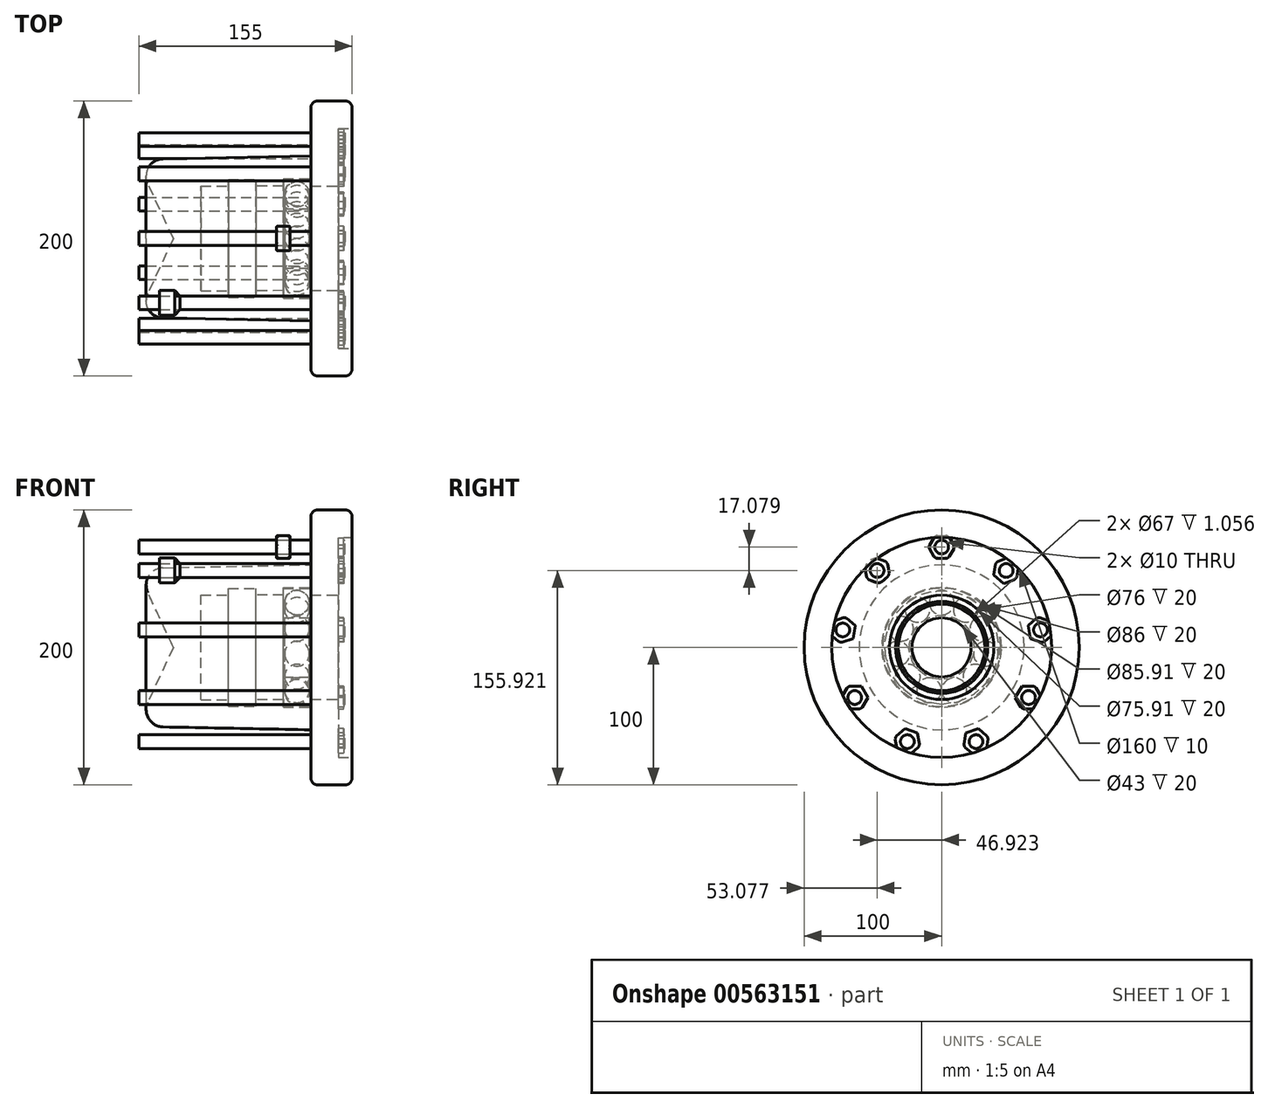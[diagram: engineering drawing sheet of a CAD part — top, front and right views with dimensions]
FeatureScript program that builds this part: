
annotation { "Feature Type Name" : "Feature", "Feature Type Description" : "" }
export const myFeature = defineFeature(function(context is Context, id is Id, definition is map)
    precondition{}
    {
        {
            var Q0;
            Q0=qCreatedBy(makeId("Front.planeOp"),FACE);
            var sketch = newSketch(context, id + "F0", { "sketchPlane" : qUnion([Q0])});
            skLineSegment(sketch, "E0", {"start": v(30, 100) * mm, "end": v(0, 100) * mm});
            skLineSegment(sketch, "E1", {"start": v(0, 100) * mm, "end": v(0, 60) * mm});
            skLineSegment(sketch, "E2.1", {"start": v(30, 80) * mm, "end": v(20, 80) * mm});
            skLineSegment(sketch, "E3", {"start": v(30, 100) * mm, "end": v(30, 80) * mm});
            skLineSegment(sketch, "E4", {"start": v(-100, 0) * mm, "end": v(-80, 0) * mm});
            skLineSegment(sketch, "E5", {"start": v(-80, 38) * mm, "end": v(-80, 0) * mm});
            skLineSegment(sketch, "E6", {"start": v(-50, 0) * mm, "end": v(-50, 38) * mm, "construction": true});
            skLineSegment(sketch, "E7", {"start": v(-80, 38) * mm, "end": v(-60, 38) * mm});
            skLineSegment(sketch, "E8", {"start": v(-60, 38) * mm, "end": v(-60, 43) * mm});
            skLineSegment(sketch, "E9", {"start": v(-60, 43) * mm, "end": v(-40, 43) * mm});
            skLineSegment(sketch, "E10", {"start": v(-40, 43) * mm, "end": v(-40, 38) * mm});
            skLineSegment(sketch, "E11", {"start": v(-20, 37.96) * mm, "end": v(-20, 42.96) * mm});
            skLineSegment(sketch, "E12", {"start": v(-20, 42.96) * mm, "end": v(0, 42.96) * mm});
            skLineSegment(sketch, "E13", {"start": v(0, 42.96) * mm, "end": v(0, 37.96) * mm});
            skLineSegment(sketch, "E14", {"start": v(0, 37.96) * mm, "end": v(20, 37.96) * mm});
            skLineSegment(sketch, "E15", {"start": v(20, 37.96) * mm, "end": v(20, 80) * mm});
            skLineSegment(sketch, "E16", {"start": v(-40, 38) * mm, "end": v(-20, 37.96) * mm});
            skLineSegment(sketch, "E17", {"start": v(0, 60) * mm, "end": v(-126.66, 57.5) * mm});
            skLineSegment(sketch, "E18", {"start": v(-126.66, 57.5) * mm, "end": v(-100, 0) * mm});
            skLineSegment(sketch, "E19", {"start": v(0, 0) * mm, "end": v(-33.89, 0) * mm, "construction": true});
            skSolve(sketch);
        }
        {
            var Q0;
            Q0=makeQuery(id+"F0.imprint","IMPRINT",FACE,{"disambiguationData":[TD([[makeQuery(id+"F0.imprint","IMPRINT",EDGE,{"derivedFrom":sQuery(id+"F0.wireOp",EDGE,"E0")}),1.0]])]});
            var Q1;
            Q1=sQuery(id+"F0.wireOp",EDGE,"E19");
            revolve(context, id + "F1", {"entities" : qUnion([Q0]), "axis" : qUnion([Q1]), "revolveType" : RevolveType.FULL});
        }
        {
            var Q0;
            Q0=makeQuery(id+"F1.opRevolve","SWEPT_EDGE",EDGE,{"disambiguationData":[OSD([sQuery(id+"F0.wireOp",EDGE,"jqeio1sC-Fs1J-a6Xr-Syng-ZmbF2VibZQXp"),sQuery(id+"F0.wireOp",EDGE,"7w0ZohrY-VkOi-IecW-S3rd-IawNJfoClKoL")])]});
            var Q1;
            Q1=makeQuery(id+"F1.opRevolve","SWEPT_EDGE",EDGE,{"disambiguationData":[OSD([sQuery(id+"F0.wireOp",EDGE,"E0"),sQuery(id+"F0.wireOp",EDGE,"E1")])]});
            var Q2;
            Q2=makeQuery(id+"F1.opRevolve","SWEPT_EDGE",EDGE,{"disambiguationData":[OSD([sQuery(id+"F0.wireOp",EDGE,"8LsLQbTB-hIyZ-haP9-eTfZ-4Z8Wfnln9Azo"),sQuery(id+"F0.wireOp",EDGE,"E0")])]});
            fillet(context, id + "F2", {"entities" : qUnion([Q0, Q1, Q2]), "radius" : 5 * mm, "tangentPropagation" : true, "allowEdgeOverflow" : false});
        }
        {
            var Q0;
            Q0=qCreatedBy(makeId("Right.planeOp"),FACE);
            var sketch = newSketch(context, id + "F3", { "sketchPlane" : qUnion([Q0])});
            skLineSegment(sketch, "E20", {"start": v(0, 0) * mm, "end": v(0, 73) * mm, "construction": true});
            skCircle(sketch, "E21", {"center": v(0, 73) * mm, "radius": 5 * mm});
            skCircle(sketch, "E22.1.0", {"center": v(-46.92, 55.92) * mm, "radius": 5 * mm});
            skCircle(sketch, "E22.2.0", {"center": v(-71.9, 12.68) * mm, "radius": 5 * mm});
            skCircle(sketch, "E22.3.0", {"center": v(-63.22, -36.5) * mm, "radius": 5 * mm});
            skCircle(sketch, "E22.4.0", {"center": v(-24.97, -68.6) * mm, "radius": 5 * mm});
            skCircle(sketch, "E22.5.0", {"center": v(24.97, -68.6) * mm, "radius": 5 * mm});
            skCircle(sketch, "E22.6.0", {"center": v(63.22, -36.5) * mm, "radius": 5 * mm});
            skCircle(sketch, "E22.7.0", {"center": v(71.9, 12.68) * mm, "radius": 5 * mm});
            skCircle(sketch, "E22.8.0", {"center": v(46.92, 55.92) * mm, "radius": 5 * mm});
            skPoint(sketch, "E22.center", {"position": v(0, 0) * mm});
            skCircle(sketch, "E23.cCircle", {"center": v(0, 73) * mm, "radius": 8.37 * mm, "construction": true});
            skLineSegment(sketch, "E23.0", {"start": v(4.83, 64.63) * mm, "end": v(-4.83, 64.63) * mm});
            skLineSegment(sketch, "E23.1", {"start": v(-4.83, 64.63) * mm, "end": v(-9.66, 73) * mm});
            skLineSegment(sketch, "E23.2", {"start": v(-9.66, 73) * mm, "end": v(-4.83, 81.37) * mm});
            skLineSegment(sketch, "E23.3", {"start": v(-4.83, 81.37) * mm, "end": v(4.83, 81.37) * mm});
            skLineSegment(sketch, "E23.4", {"start": v(4.83, 81.37) * mm, "end": v(9.66, 73) * mm});
            skLineSegment(sketch, "E23.5", {"start": v(9.66, 73) * mm, "end": v(4.83, 64.63) * mm});
            skPoint(sketch, "E23.0.midPoint", {"position": v(0, 64.63) * mm});
            skCircle(sketch, "E24.1.0", {"center": v(-63.22, -36.5) * mm, "radius": 8.37 * mm, "construction": true});
            skLineSegment(sketch, "E24.1.1", {"start": v(-68.05, -44.87) * mm, "end": v(-72.88, -36.5) * mm});
            skLineSegment(sketch, "E24.1.2", {"start": v(-58.39, -44.87) * mm, "end": v(-68.05, -44.87) * mm});
            skLineSegment(sketch, "E24.1.3", {"start": v(-72.88, -36.5) * mm, "end": v(-68.05, -28.13) * mm});
            skCircle(sketch, "E24.2.0", {"center": v(63.22, -36.5) * mm, "radius": 8.37 * mm, "construction": true});
            skLineSegment(sketch, "E24.2.1", {"start": v(72.88, -36.5) * mm, "end": v(68.05, -44.87) * mm});
            skLineSegment(sketch, "E24.2.2", {"start": v(68.05, -28.13) * mm, "end": v(72.88, -36.5) * mm});
            skLineSegment(sketch, "E24.2.3", {"start": v(68.05, -44.87) * mm, "end": v(58.39, -44.87) * mm});
            skLineSegment(sketch, "E25.1.0", {"start": v(-37.84, 52.62) * mm, "end": v(-45.25, 46.4) * mm});
            skLineSegment(sketch, "E25.1.1", {"start": v(-48.6, 65.44) * mm, "end": v(-39.52, 62.13) * mm});
            skCircle(sketch, "E25.1.2", {"center": v(-46.92, 55.92) * mm, "radius": 8.37 * mm, "construction": true});
            skLineSegment(sketch, "E25.1.4", {"start": v(-54.32, 49.71) * mm, "end": v(-56, 59.23) * mm});
            skLineSegment(sketch, "E25.1.5", {"start": v(-56, 59.23) * mm, "end": v(-48.6, 65.44) * mm});
            skLineSegment(sketch, "E25.1.6", {"start": v(-39.52, 62.13) * mm, "end": v(-37.84, 52.62) * mm});
            skLineSegment(sketch, "E25.1.7", {"start": v(-45.25, 46.4) * mm, "end": v(-54.32, 49.71) * mm});
            skPoint(sketch, "E25.1.8", {"position": v(-41.55, 49.51) * mm});
            skLineSegment(sketch, "E25.2.0", {"start": v(-62.81, 15.98) * mm, "end": v(-64.5, 6.47) * mm});
            skLineSegment(sketch, "E25.2.1", {"start": v(-79.3, 18.89) * mm, "end": v(-70.21, 22.2) * mm});
            skCircle(sketch, "E25.2.2", {"center": v(-71.9, 12.68) * mm, "radius": 8.37 * mm, "construction": true});
            skLineSegment(sketch, "E25.2.4", {"start": v(-73.57, 3.16) * mm, "end": v(-80.97, 9.37) * mm});
            skLineSegment(sketch, "E25.2.5", {"start": v(-80.97, 9.37) * mm, "end": v(-79.3, 18.89) * mm});
            skLineSegment(sketch, "E25.2.6", {"start": v(-70.21, 22.2) * mm, "end": v(-62.81, 15.98) * mm});
            skLineSegment(sketch, "E25.2.7", {"start": v(-64.5, 6.47) * mm, "end": v(-73.57, 3.16) * mm});
            skPoint(sketch, "E25.2.8", {"position": v(-63.65, 11.22) * mm});
            skLineSegment(sketch, "E25.3.0", {"start": v(-58.39, -28.13) * mm, "end": v(-53.56, -36.5) * mm});
            skLineSegment(sketch, "E25.3.6", {"start": v(-68.05, -28.13) * mm, "end": v(-58.39, -28.13) * mm});
            skLineSegment(sketch, "E25.3.7", {"start": v(-53.56, -36.5) * mm, "end": v(-58.39, -44.87) * mm});
            skPoint(sketch, "E25.3.8", {"position": v(-55.97, -32.32) * mm});
            skLineSegment(sketch, "E25.4.0", {"start": v(-26.65, -59.08) * mm, "end": v(-17.57, -62.39) * mm});
            skLineSegment(sketch, "E25.4.1", {"start": v(-32.37, -74.8) * mm, "end": v(-34.05, -65.3) * mm});
            skCircle(sketch, "E25.4.2", {"center": v(-24.97, -68.6) * mm, "radius": 8.37 * mm, "construction": true});
            skLineSegment(sketch, "E25.4.4", {"start": v(-15.89, -71.9) * mm, "end": v(-23.29, -78.11) * mm});
            skLineSegment(sketch, "E25.4.5", {"start": v(-23.29, -78.11) * mm, "end": v(-32.37, -74.8) * mm});
            skLineSegment(sketch, "E25.4.6", {"start": v(-34.05, -65.3) * mm, "end": v(-26.65, -59.08) * mm});
            skLineSegment(sketch, "E25.4.7", {"start": v(-17.57, -62.39) * mm, "end": v(-15.89, -71.9) * mm});
            skPoint(sketch, "E25.4.8", {"position": v(-22.1, -60.74) * mm});
            skLineSegment(sketch, "E25.5.0", {"start": v(17.57, -62.39) * mm, "end": v(26.65, -59.08) * mm});
            skLineSegment(sketch, "E25.5.1", {"start": v(23.29, -78.11) * mm, "end": v(15.89, -71.9) * mm});
            skCircle(sketch, "E25.5.2", {"center": v(24.97, -68.6) * mm, "radius": 8.37 * mm, "construction": true});
            skLineSegment(sketch, "E25.5.4", {"start": v(34.05, -65.3) * mm, "end": v(32.37, -74.8) * mm});
            skLineSegment(sketch, "E25.5.5", {"start": v(32.37, -74.8) * mm, "end": v(23.29, -78.11) * mm});
            skLineSegment(sketch, "E25.5.6", {"start": v(15.89, -71.9) * mm, "end": v(17.57, -62.39) * mm});
            skLineSegment(sketch, "E25.5.7", {"start": v(26.65, -59.08) * mm, "end": v(34.05, -65.3) * mm});
            skPoint(sketch, "E25.5.8", {"position": v(22.1, -60.74) * mm});
            skLineSegment(sketch, "E25.6.0", {"start": v(53.56, -36.5) * mm, "end": v(58.39, -28.13) * mm});
            skLineSegment(sketch, "E25.6.6", {"start": v(58.39, -44.87) * mm, "end": v(53.56, -36.5) * mm});
            skLineSegment(sketch, "E25.6.7", {"start": v(58.39, -28.13) * mm, "end": v(68.05, -28.13) * mm});
            skPoint(sketch, "E25.6.8", {"position": v(55.97, -32.32) * mm});
            skLineSegment(sketch, "E25.7.0", {"start": v(64.5, 6.47) * mm, "end": v(62.81, 15.98) * mm});
            skLineSegment(sketch, "E25.7.1", {"start": v(80.97, 9.37) * mm, "end": v(73.57, 3.16) * mm});
            skCircle(sketch, "E25.7.2", {"center": v(71.9, 12.68) * mm, "radius": 8.37 * mm, "construction": true});
            skLineSegment(sketch, "E25.7.4", {"start": v(70.21, 22.2) * mm, "end": v(79.3, 18.89) * mm});
            skLineSegment(sketch, "E25.7.5", {"start": v(79.3, 18.89) * mm, "end": v(80.97, 9.37) * mm});
            skLineSegment(sketch, "E25.7.6", {"start": v(73.57, 3.16) * mm, "end": v(64.5, 6.47) * mm});
            skLineSegment(sketch, "E25.7.7", {"start": v(62.81, 15.98) * mm, "end": v(70.21, 22.2) * mm});
            skPoint(sketch, "E25.7.8", {"position": v(63.65, 11.22) * mm});
            skLineSegment(sketch, "E25.8.0", {"start": v(45.25, 46.4) * mm, "end": v(37.84, 52.62) * mm});
            skLineSegment(sketch, "E25.8.1", {"start": v(56, 59.23) * mm, "end": v(54.32, 49.71) * mm});
            skCircle(sketch, "E25.8.2", {"center": v(46.92, 55.92) * mm, "radius": 8.37 * mm, "construction": true});
            skLineSegment(sketch, "E25.8.4", {"start": v(39.52, 62.13) * mm, "end": v(48.6, 65.44) * mm});
            skLineSegment(sketch, "E25.8.5", {"start": v(48.6, 65.44) * mm, "end": v(56, 59.23) * mm});
            skLineSegment(sketch, "E25.8.6", {"start": v(54.32, 49.71) * mm, "end": v(45.25, 46.4) * mm});
            skLineSegment(sketch, "E25.8.7", {"start": v(37.84, 52.62) * mm, "end": v(39.52, 62.13) * mm});
            skPoint(sketch, "E25.8.8", {"position": v(41.55, 49.51) * mm});
            skCircle(sketch, "E26", {"center": v(0, 73) * mm, "radius": 9 * mm});
            skCircle(sketch, "E27.1.0", {"center": v(-46.92, 55.92) * mm, "radius": 9 * mm});
            skCircle(sketch, "E27.2.0", {"center": v(-71.9, 12.68) * mm, "radius": 9 * mm});
            skCircle(sketch, "E27.3.0", {"center": v(-63.22, -36.5) * mm, "radius": 9 * mm});
            skCircle(sketch, "E27.4.0", {"center": v(-24.97, -68.6) * mm, "radius": 9 * mm});
            skCircle(sketch, "E27.5.0", {"center": v(24.97, -68.6) * mm, "radius": 9 * mm});
            skCircle(sketch, "E27.6.0", {"center": v(63.22, -36.5) * mm, "radius": 9 * mm});
            skCircle(sketch, "E27.7.0", {"center": v(71.9, 12.68) * mm, "radius": 9 * mm});
            skCircle(sketch, "E27.8.0", {"center": v(46.92, 55.92) * mm, "radius": 9 * mm});
            skSolve(sketch);
        }
        {
            var Q0;
            Q0=makeQuery(id+"F3.imprint","IMPRINT",FACE,{"disambiguationData":[TD([[makeQuery(id+"F3.imprint","IMPRINT",EDGE,{"derivedFrom":sQuery(id+"F3.wireOp",EDGE,"E22.6.0")}),1.0]])]});
            var Q1;
            Q1=makeQuery(id+"F3.imprint","IMPRINT",FACE,{"disambiguationData":[TD([[makeQuery(id+"F3.imprint","IMPRINT",EDGE,{"derivedFrom":sQuery(id+"F3.wireOp",EDGE,"E22.7.0")}),1.0]])]});
            var Q2;
            Q2=makeQuery(id+"F3.imprint","IMPRINT",FACE,{"disambiguationData":[TD([[makeQuery(id+"F3.imprint","IMPRINT",EDGE,{"derivedFrom":sQuery(id+"F3.wireOp",EDGE,"E22.8.0")}),1.0]])]});
            var Q3;
            Q3=makeQuery(id+"F3.imprint","IMPRINT",FACE,{"disambiguationData":[TD([[makeQuery(id+"F3.imprint","IMPRINT",EDGE,{"derivedFrom":sQuery(id+"F3.wireOp",EDGE,"E21")}),1.0]])]});
            var Q4;
            Q4=makeQuery(id+"F3.imprint","IMPRINT",FACE,{"disambiguationData":[TD([[makeQuery(id+"F3.imprint","IMPRINT",EDGE,{"derivedFrom":sQuery(id+"F3.wireOp",EDGE,"E22.1.0")}),1.0]])]});
            var Q5;
            Q5=makeQuery(id+"F3.imprint","IMPRINT",FACE,{"disambiguationData":[TD([[makeQuery(id+"F3.imprint","IMPRINT",EDGE,{"derivedFrom":sQuery(id+"F3.wireOp",EDGE,"E22.2.0")}),1.0]])]});
            var Q6;
            Q6=makeQuery(id+"F3.imprint","IMPRINT",FACE,{"disambiguationData":[TD([[makeQuery(id+"F3.imprint","IMPRINT",EDGE,{"derivedFrom":sQuery(id+"F3.wireOp",EDGE,"E22.3.0")}),1.0]])]});
            var Q7;
            Q7=makeQuery(id+"F3.imprint","IMPRINT",FACE,{"disambiguationData":[TD([[makeQuery(id+"F3.imprint","IMPRINT",EDGE,{"derivedFrom":sQuery(id+"F3.wireOp",EDGE,"E22.5.0")}),1.0]])]});
            var Q8;
            Q8=makeQuery(id+"F3.imprint","IMPRINT",FACE,{"disambiguationData":[TD([[makeQuery(id+"F3.imprint","IMPRINT",EDGE,{"derivedFrom":sQuery(id+"F3.wireOp",EDGE,"E22.4.0")}),1.0]])]});
            extrude(context, id + "F4", {"entities" : qUnion([Q0, Q1, Q2, Q3, Q4, Q5, Q6, Q7, Q8]), "operationType" : NewBodyOperationType.ADD, "oppositeDirection" : true, "depth" : 125 * mm, "offsetDistance" : 25 * mm, "hasSecondDirection" : true, "secondDirectionOppositeDirection" : false, "secondDirectionDepth" : 25 * mm});
        }
        {
            var Q0;
            Q0=makeQuery(id+"F3.imprint","IMPRINT",FACE,{"disambiguationData":[TD([[makeQuery(id+"F3.imprint","IMPRINT",EDGE,{"derivedFrom":sQuery(id+"F3.wireOp",EDGE,"E21")}),-1.0]])]});
            var Q1;
            {var subQ0=sQuery(id+"F3.wireOp",EDGE,"E25.2.6");var subQ1=sQuery(id+"F3.wireOp",EDGE,"E25.2.0");var subQ2=makeQuery(id+"F3.imprint","INTERSECT",VERTEX,{"derivedFrom":[subQ1,subQ0]});Q1=makeQuery(id+"F3.imprint","IMPRINT",FACE,{"disambiguationData":[TD([[makeQuery(id+"F3.imprint","IMPRINT",EDGE,{"disambiguationData":[TD([[subQ2,-1.0]])],"derivedFrom":subQ1}),-1.0]])]});}
            var Q2;
            {var subQ0=sQuery(id+"F3.wireOp",EDGE,"E25.2.7");var subQ1=sQuery(id+"F3.wireOp",EDGE,"E25.2.0");var subQ2=makeQuery(id+"F3.imprint","INTERSECT",VERTEX,{"derivedFrom":[subQ1,subQ0]});Q2=makeQuery(id+"F3.imprint","IMPRINT",FACE,{"disambiguationData":[TD([[makeQuery(id+"F3.imprint","IMPRINT",EDGE,{"disambiguationData":[TD([[subQ2,1.0]])],"derivedFrom":subQ1}),-1.0]])]});}
            var Q3;
            {var subQ0=sQuery(id+"F3.wireOp",EDGE,"E25.3.6");var subQ1=sQuery(id+"F3.wireOp",EDGE,"E25.3.0");var subQ2=makeQuery(id+"F3.imprint","INTERSECT",VERTEX,{"derivedFrom":[subQ1,subQ0]});Q3=makeQuery(id+"F3.imprint","IMPRINT",FACE,{"disambiguationData":[TD([[makeQuery(id+"F3.imprint","IMPRINT",EDGE,{"disambiguationData":[TD([[subQ2,-1.0]])],"derivedFrom":subQ1}),-1.0]])]});}
            var Q4;
            {var subQ0=sQuery(id+"F3.wireOp",EDGE,"E25.3.7");var subQ1=sQuery(id+"F3.wireOp",EDGE,"E25.3.0");var subQ2=makeQuery(id+"F3.imprint","INTERSECT",VERTEX,{"derivedFrom":[subQ1,subQ0]});Q4=makeQuery(id+"F3.imprint","IMPRINT",FACE,{"disambiguationData":[TD([[makeQuery(id+"F3.imprint","IMPRINT",EDGE,{"disambiguationData":[TD([[subQ2,1.0]])],"derivedFrom":subQ1}),-1.0]])]});}
            var Q5;
            {var subQ0=sQuery(id+"F3.wireOp",EDGE,"E25.4.6");var subQ1=sQuery(id+"F3.wireOp",EDGE,"E25.4.0");var subQ2=makeQuery(id+"F3.imprint","INTERSECT",VERTEX,{"derivedFrom":[subQ1,subQ0]});Q5=makeQuery(id+"F3.imprint","IMPRINT",FACE,{"disambiguationData":[TD([[makeQuery(id+"F3.imprint","IMPRINT",EDGE,{"disambiguationData":[TD([[subQ2,-1.0]])],"derivedFrom":subQ1}),-1.0]])]});}
            var Q6;
            {var subQ0=sQuery(id+"F3.wireOp",EDGE,"E25.4.7");var subQ1=sQuery(id+"F3.wireOp",EDGE,"E25.4.0");var subQ2=makeQuery(id+"F3.imprint","INTERSECT",VERTEX,{"derivedFrom":[subQ1,subQ0]});Q6=makeQuery(id+"F3.imprint","IMPRINT",FACE,{"disambiguationData":[TD([[makeQuery(id+"F3.imprint","IMPRINT",EDGE,{"disambiguationData":[TD([[subQ2,1.0]])],"derivedFrom":subQ1}),-1.0]])]});}
            var Q7;
            {var subQ0=sQuery(id+"F3.wireOp",EDGE,"E25.5.6");var subQ1=sQuery(id+"F3.wireOp",EDGE,"E25.5.0");var subQ2=makeQuery(id+"F3.imprint","INTERSECT",VERTEX,{"derivedFrom":[subQ1,subQ0]});Q7=makeQuery(id+"F3.imprint","IMPRINT",FACE,{"disambiguationData":[TD([[makeQuery(id+"F3.imprint","IMPRINT",EDGE,{"disambiguationData":[TD([[subQ2,-1.0]])],"derivedFrom":subQ1}),-1.0]])]});}
            var Q8;
            {var subQ0=sQuery(id+"F3.wireOp",EDGE,"E25.5.7");var subQ1=sQuery(id+"F3.wireOp",EDGE,"E25.5.0");var subQ2=makeQuery(id+"F3.imprint","INTERSECT",VERTEX,{"derivedFrom":[subQ1,subQ0]});Q8=makeQuery(id+"F3.imprint","IMPRINT",FACE,{"disambiguationData":[TD([[makeQuery(id+"F3.imprint","IMPRINT",EDGE,{"disambiguationData":[TD([[subQ2,1.0]])],"derivedFrom":subQ1}),-1.0]])]});}
            var Q9;
            {var subQ0=sQuery(id+"F3.wireOp",EDGE,"E25.6.6");var subQ1=sQuery(id+"F3.wireOp",EDGE,"E25.6.0");var subQ2=makeQuery(id+"F3.imprint","INTERSECT",VERTEX,{"derivedFrom":[subQ1,subQ0]});Q9=makeQuery(id+"F3.imprint","IMPRINT",FACE,{"disambiguationData":[TD([[makeQuery(id+"F3.imprint","IMPRINT",EDGE,{"disambiguationData":[TD([[subQ2,-1.0]])],"derivedFrom":subQ1}),-1.0]])]});}
            var Q10;
            {var subQ0=sQuery(id+"F3.wireOp",EDGE,"E25.6.7");var subQ1=sQuery(id+"F3.wireOp",EDGE,"E25.6.0");var subQ2=makeQuery(id+"F3.imprint","INTERSECT",VERTEX,{"derivedFrom":[subQ1,subQ0]});Q10=makeQuery(id+"F3.imprint","IMPRINT",FACE,{"disambiguationData":[TD([[makeQuery(id+"F3.imprint","IMPRINT",EDGE,{"disambiguationData":[TD([[subQ2,1.0]])],"derivedFrom":subQ1}),-1.0]])]});}
            var Q11;
            {var subQ0=sQuery(id+"F3.wireOp",EDGE,"E25.7.6");var subQ1=sQuery(id+"F3.wireOp",EDGE,"E25.7.0");var subQ2=makeQuery(id+"F3.imprint","INTERSECT",VERTEX,{"derivedFrom":[subQ1,subQ0]});Q11=makeQuery(id+"F3.imprint","IMPRINT",FACE,{"disambiguationData":[TD([[makeQuery(id+"F3.imprint","IMPRINT",EDGE,{"disambiguationData":[TD([[subQ2,-1.0]])],"derivedFrom":subQ1}),-1.0]])]});}
            var Q12;
            {var subQ0=sQuery(id+"F3.wireOp",EDGE,"E25.7.7");var subQ1=sQuery(id+"F3.wireOp",EDGE,"E25.7.0");var subQ2=makeQuery(id+"F3.imprint","INTERSECT",VERTEX,{"derivedFrom":[subQ1,subQ0]});Q12=makeQuery(id+"F3.imprint","IMPRINT",FACE,{"disambiguationData":[TD([[makeQuery(id+"F3.imprint","IMPRINT",EDGE,{"disambiguationData":[TD([[subQ2,1.0]])],"derivedFrom":subQ1}),-1.0]])]});}
            var Q13;
            {var subQ0=sQuery(id+"F3.wireOp",EDGE,"E25.8.6");var subQ1=sQuery(id+"F3.wireOp",EDGE,"E25.8.0");var subQ2=makeQuery(id+"F3.imprint","INTERSECT",VERTEX,{"derivedFrom":[subQ1,subQ0]});Q13=makeQuery(id+"F3.imprint","IMPRINT",FACE,{"disambiguationData":[TD([[makeQuery(id+"F3.imprint","IMPRINT",EDGE,{"disambiguationData":[TD([[subQ2,-1.0]])],"derivedFrom":subQ1}),-1.0]])]});}
            var Q14;
            {var subQ0=sQuery(id+"F3.wireOp",EDGE,"E25.8.7");var subQ1=sQuery(id+"F3.wireOp",EDGE,"E25.8.0");var subQ2=makeQuery(id+"F3.imprint","INTERSECT",VERTEX,{"derivedFrom":[subQ1,subQ0]});Q14=makeQuery(id+"F3.imprint","IMPRINT",FACE,{"disambiguationData":[TD([[makeQuery(id+"F3.imprint","IMPRINT",EDGE,{"disambiguationData":[TD([[subQ2,1.0]])],"derivedFrom":subQ1}),-1.0]])]});}
            var Q15;
            Q15=makeQuery(id+"F3.imprint","IMPRINT",FACE,{"disambiguationData":[TD([[makeQuery(id+"F3.imprint","IMPRINT",EDGE,{"derivedFrom":sQuery(id+"F3.wireOp",EDGE,"E22.1.0")}),-1.0]])]});
            var Q16;
            Q16=makeQuery(id+"F3.imprint","IMPRINT",FACE,{"disambiguationData":[TD([[makeQuery(id+"F3.imprint","IMPRINT",EDGE,{"derivedFrom":sQuery(id+"F3.wireOp",EDGE,"E22.2.0")}),-1.0]])]});
            var Q17;
            Q17=makeQuery(id+"F3.imprint","IMPRINT",FACE,{"disambiguationData":[TD([[makeQuery(id+"F3.imprint","IMPRINT",EDGE,{"derivedFrom":sQuery(id+"F3.wireOp",EDGE,"E22.3.0")}),-1.0]])]});
            var Q18;
            Q18=makeQuery(id+"F3.imprint","IMPRINT",FACE,{"disambiguationData":[TD([[makeQuery(id+"F3.imprint","IMPRINT",EDGE,{"derivedFrom":sQuery(id+"F3.wireOp",EDGE,"E22.4.0")}),-1.0]])]});
            var Q19;
            Q19=makeQuery(id+"F3.imprint","IMPRINT",FACE,{"disambiguationData":[TD([[makeQuery(id+"F3.imprint","IMPRINT",EDGE,{"derivedFrom":sQuery(id+"F3.wireOp",EDGE,"E22.5.0")}),-1.0]])]});
            var Q20;
            Q20=makeQuery(id+"F3.imprint","IMPRINT",FACE,{"disambiguationData":[TD([[makeQuery(id+"F3.imprint","IMPRINT",EDGE,{"derivedFrom":sQuery(id+"F3.wireOp",EDGE,"E22.6.0")}),-1.0]])]});
            var Q21;
            Q21=makeQuery(id+"F3.imprint","IMPRINT",FACE,{"disambiguationData":[TD([[makeQuery(id+"F3.imprint","IMPRINT",EDGE,{"derivedFrom":sQuery(id+"F3.wireOp",EDGE,"E22.7.0")}),-1.0]])]});
            var Q22;
            Q22=makeQuery(id+"F3.imprint","IMPRINT",FACE,{"disambiguationData":[TD([[makeQuery(id+"F3.imprint","IMPRINT",EDGE,{"derivedFrom":sQuery(id+"F3.wireOp",EDGE,"E22.8.0")}),-1.0]])]});
            extrude(context, id + "F5", {"entities" : qUnion([Q0, Q1, Q2, Q3, Q4, Q5, Q6, Q7, Q8, Q9, Q10, Q11, Q12, Q13, Q14, Q15, Q16, Q17, Q18, Q19, Q20, Q21, Q22]), "operationType" : NewBodyOperationType.ADD, "depth" : 24 * mm, "offsetDistance" : 25 * mm});
        }
        {
            var Q0;
            Q0=makeQuery(id+"F1.opRevolve","SWEPT_EDGE",EDGE,{"disambiguationData":[OSD([sQuery(id+"F0.wireOp",EDGE,"E17"),sQuery(id+"F0.wireOp",EDGE,"E18")])]});
            fillet(context, id + "F6", {"entities" : qUnion([Q0]), "radius" : 12.5 * mm, "tangentPropagation" : true, "allowEdgeOverflow" : false});
        }
        {
            var Q0;
            {var subQ0=sQuery(id+"F3.wireOp",EDGE,"E27.1.0");var subQ1=sQuery(id+"F3.wireOp",EDGE,"E25.1.6");var subQ2=makeQuery(id+"F3.imprint","INTERSECT",VERTEX,{"disambiguationData":[OD(0.0)],"derivedFrom":[subQ1,subQ0]});Q0=makeQuery(id+"F3.imprint","IMPRINT",FACE,{"disambiguationData":[TD([[makeQuery(id+"F3.imprint","IMPRINT",EDGE,{"disambiguationData":[TD([[subQ2,-1.0]])],"derivedFrom":subQ1}),1.0]])]});}
            var Q1;
            {var subQ0=sQuery(id+"F3.wireOp",EDGE,"E27.1.0");var subQ1=sQuery(id+"F3.wireOp",EDGE,"E25.1.1");var subQ2=makeQuery(id+"F3.imprint","INTERSECT",VERTEX,{"disambiguationData":[OD(0.0)],"derivedFrom":[subQ1,subQ0]});Q1=makeQuery(id+"F3.imprint","IMPRINT",FACE,{"disambiguationData":[TD([[makeQuery(id+"F3.imprint","IMPRINT",EDGE,{"disambiguationData":[TD([[subQ2,-1.0]])],"derivedFrom":subQ1}),1.0]])]});}
            var Q2;
            {var subQ0=sQuery(id+"F3.wireOp",EDGE,"E27.1.0");var subQ1=sQuery(id+"F3.wireOp",EDGE,"E25.1.5");var subQ2=makeQuery(id+"F3.imprint","INTERSECT",VERTEX,{"disambiguationData":[OD(0.0)],"derivedFrom":[subQ1,subQ0]});Q2=makeQuery(id+"F3.imprint","IMPRINT",FACE,{"disambiguationData":[TD([[makeQuery(id+"F3.imprint","IMPRINT",EDGE,{"disambiguationData":[TD([[subQ2,-1.0]])],"derivedFrom":subQ1}),1.0]])]});}
            var Q3;
            {var subQ0=sQuery(id+"F3.wireOp",EDGE,"E27.1.0");var subQ1=sQuery(id+"F3.wireOp",EDGE,"E25.1.4");var subQ2=makeQuery(id+"F3.imprint","INTERSECT",VERTEX,{"disambiguationData":[OD(0.0)],"derivedFrom":[subQ1,subQ0]});Q3=makeQuery(id+"F3.imprint","IMPRINT",FACE,{"disambiguationData":[TD([[makeQuery(id+"F3.imprint","IMPRINT",EDGE,{"disambiguationData":[TD([[subQ2,-1.0]])],"derivedFrom":subQ1}),1.0]])]});}
            var Q4;
            {var subQ0=sQuery(id+"F3.wireOp",EDGE,"E27.1.0");var subQ1=sQuery(id+"F3.wireOp",EDGE,"E25.1.7");var subQ2=makeQuery(id+"F3.imprint","INTERSECT",VERTEX,{"disambiguationData":[OD(0.0)],"derivedFrom":[subQ1,subQ0]});Q4=makeQuery(id+"F3.imprint","IMPRINT",FACE,{"disambiguationData":[TD([[makeQuery(id+"F3.imprint","IMPRINT",EDGE,{"disambiguationData":[TD([[subQ2,-1.0]])],"derivedFrom":subQ1}),1.0]])]});}
            var Q5;
            Q5=makeQuery(id+"F3.imprint","IMPRINT",FACE,{"disambiguationData":[TD([[makeQuery(id+"F3.imprint","IMPRINT",EDGE,{"derivedFrom":sQuery(id+"F3.wireOp",EDGE,"E22.1.0")}),-1.0]])]});
            var Q6;
            {var subQ0=sQuery(id+"F3.wireOp",EDGE,"E27.1.0");var subQ1=sQuery(id+"F3.wireOp",EDGE,"E25.1.0");var subQ2=makeQuery(id+"F3.imprint","INTERSECT",VERTEX,{"disambiguationData":[OD(0.0)],"derivedFrom":[subQ1,subQ0]});Q6=makeQuery(id+"F3.imprint","IMPRINT",FACE,{"disambiguationData":[TD([[makeQuery(id+"F3.imprint","IMPRINT",EDGE,{"disambiguationData":[TD([[subQ2,-1.0]])],"derivedFrom":subQ1}),1.0]])]});}
            extrude(context, id + "F7", {"entities" : qUnion([Q0, Q1, Q2, Q3, Q4, Q5, Q6]), "oppositeDirection" : true, "depth" : 110 * mm, "offsetDistance" : 25 * mm, "hasSecondDirection" : true, "secondDirectionOppositeDirection" : true, "secondDirectionDepth" : 95 * mm});
        }
        {
            var Q0;
            Q0=makeQuery(id+"F7.opExtrude","CAP_EDGE",EDGE,{"disambiguationData":[OSD([sQuery(id+"F3.wireOp",EDGE,"E27.1.0")])],"isStart":true});
            chamfer(context, id + "F8", {"entities" : qUnion([Q0]), "width" : 4 * mm, "tangentPropagation" : true});
        }
        {
            var Q0;
            Q0=makeQuery(id+"F3.imprint","IMPRINT",FACE,{"disambiguationData":[TD([[makeQuery(id+"F3.imprint","IMPRINT",EDGE,{"derivedFrom":sQuery(id+"F3.wireOp",EDGE,"E21")}),-1.0]])]});
            extrude(context, id + "F9", {"entities" : qUnion([Q0]), "oppositeDirection" : true, "depth" : 25 * mm, "offsetDistance" : 25 * mm, "hasSecondDirection" : true, "secondDirectionOppositeDirection" : true, "secondDirectionDepth" : 15 * mm});
        }
        {
            var Q0;
            Q0=makeQuery(id+"F9.opExtrude","CAP_FACE",FACE,{"disambiguationData":[OSD([sQuery(id+"F3.wireOp",EDGE,"E21"),sQuery(id+"F3.wireOp",EDGE,"E23.0"),sQuery(id+"F3.wireOp",EDGE,"E23.1"),sQuery(id+"F3.wireOp",EDGE,"E23.2"),sQuery(id+"F3.wireOp",EDGE,"E23.3"),sQuery(id+"F3.wireOp",EDGE,"E23.4"),sQuery(id+"F3.wireOp",EDGE,"E23.5"),sQuery(id+"F3.wireOp",EDGE,"E26")])],"isStart":false});
            var Q1;
            Q1=makeQuery(id+"F9.opExtrude","CAP_FACE",FACE,{"disambiguationData":[OSD([sQuery(id+"F3.wireOp",EDGE,"E21"),sQuery(id+"F3.wireOp",EDGE,"E23.0"),sQuery(id+"F3.wireOp",EDGE,"E23.1"),sQuery(id+"F3.wireOp",EDGE,"E23.2"),sQuery(id+"F3.wireOp",EDGE,"E23.3"),sQuery(id+"F3.wireOp",EDGE,"E23.4"),sQuery(id+"F3.wireOp",EDGE,"E23.5"),sQuery(id+"F3.wireOp",EDGE,"E26")])],"isStart":true});
            fillet(context, id + "F10", {"entities" : qUnion([Q0, Q1]), "radius" : 1 * mm, "tangentPropagation" : true, "allowEdgeOverflow" : false});
        }
        {
            var Q0;
            {var subQ0=sQuery(id+"F3.wireOp",EDGE,"E26");var subQ1=sQuery(id+"F3.wireOp",EDGE,"E23.3");Q0=makeQuery(id+"F9.opExtrude","SWEPT_EDGE",EDGE,{"disambiguationData":[OSD([subQ1,subQ0]),TDD([makeQuery(id+"F3.imprint","INTERSECT",VERTEX,{"disambiguationData":[OD(0.0)],"derivedFrom":[subQ1,subQ0]})])]});}
            var Q1;
            {var subQ0=sQuery(id+"F3.wireOp",EDGE,"E26");var subQ1=sQuery(id+"F3.wireOp",EDGE,"E23.2");Q1=makeQuery(id+"F9.opExtrude","SWEPT_EDGE",EDGE,{"disambiguationData":[OSD([subQ1,subQ0]),TDD([makeQuery(id+"F3.imprint","INTERSECT",VERTEX,{"disambiguationData":[OD(1.0)],"derivedFrom":[subQ1,subQ0]})])]});}
            var Q2;
            {var subQ0=sQuery(id+"F3.wireOp",EDGE,"E26");var subQ1=sQuery(id+"F3.wireOp",EDGE,"E23.2");Q2=makeQuery(id+"F9.opExtrude","SWEPT_EDGE",EDGE,{"disambiguationData":[OSD([subQ1,subQ0]),TDD([makeQuery(id+"F3.imprint","INTERSECT",VERTEX,{"disambiguationData":[OD(0.0)],"derivedFrom":[subQ1,subQ0]})])]});}
            var Q3;
            {var subQ0=sQuery(id+"F3.wireOp",EDGE,"E26");var subQ1=sQuery(id+"F3.wireOp",EDGE,"E23.1");Q3=makeQuery(id+"F9.opExtrude","SWEPT_EDGE",EDGE,{"disambiguationData":[OSD([subQ1,subQ0]),TDD([makeQuery(id+"F3.imprint","INTERSECT",VERTEX,{"disambiguationData":[OD(1.0)],"derivedFrom":[subQ1,subQ0]})])]});}
            var Q4;
            {var subQ0=sQuery(id+"F3.wireOp",EDGE,"E26");var subQ1=makeQuery(id+"F3.imprint","IMPRINT",EDGE,{"disambiguationData":[TD([[makeQuery(id+"F3.imprint","INTERSECT",VERTEX,{"disambiguationData":[OD(1.0)],"derivedFrom":[sQuery(id+"F3.wireOp",EDGE,"E23.1"),subQ0]}),1.0]])],"derivedFrom":subQ0});Q4=makeQuery(id+"F10.opFillet","BLEND_EDGE",EDGE,{"blendedFrom":[makeQuery(id+"F9.opExtrude","CAP_EDGE",EDGE,{"disambiguationData":[OSD([subQ0]),TDD([subQ1])],"isStart":false}),makeQuery(id+"F9.opExtrude","SWEPT_FACE",FACE,{"disambiguationData":[OSD([subQ0]),TDD([subQ1])]})],"blendedInto":[makeQuery(id+"F9.opExtrude","SWEPT_FACE",FACE,{"disambiguationData":[OSD([subQ0]),TDD([subQ1])]})]});}
            var Q5;
            {var subQ0=sQuery(id+"F3.wireOp",EDGE,"E26");var subQ1=makeQuery(id+"F3.imprint","IMPRINT",EDGE,{"disambiguationData":[TD([[makeQuery(id+"F3.imprint","INTERSECT",VERTEX,{"disambiguationData":[OD(1.0)],"derivedFrom":[sQuery(id+"F3.wireOp",EDGE,"E23.1"),subQ0]}),1.0]])],"derivedFrom":subQ0});Q5=makeQuery(id+"F10.opFillet","BLEND_EDGE",EDGE,{"blendedFrom":[makeQuery(id+"F9.opExtrude","CAP_EDGE",EDGE,{"disambiguationData":[OSD([subQ0]),TDD([subQ1])],"isStart":true}),makeQuery(id+"F9.opExtrude","SWEPT_FACE",FACE,{"disambiguationData":[OSD([subQ0]),TDD([subQ1])]})],"blendedInto":[makeQuery(id+"F9.opExtrude","SWEPT_FACE",FACE,{"disambiguationData":[OSD([subQ0]),TDD([subQ1])]})]});}
            var Q6;
            {var subQ0=sQuery(id+"F3.wireOp",EDGE,"E26");Q6=makeQuery(id+"F9.opExtrude","SWEPT_FACE",FACE,{"disambiguationData":[OSD([subQ0]),TDD([makeQuery(id+"F3.imprint","IMPRINT",EDGE,{"disambiguationData":[TD([[makeQuery(id+"F3.imprint","INTERSECT",VERTEX,{"disambiguationData":[OD(1.0)],"derivedFrom":[sQuery(id+"F3.wireOp",EDGE,"E23.2"),subQ0]}),1.0]])],"derivedFrom":subQ0})])]});}
            var Q7;
            {var subQ0=sQuery(id+"F3.wireOp",EDGE,"E26");Q7=makeQuery(id+"F9.opExtrude","SWEPT_FACE",FACE,{"disambiguationData":[OSD([subQ0]),TDD([makeQuery(id+"F3.imprint","IMPRINT",EDGE,{"disambiguationData":[TD([[makeQuery(id+"F3.imprint","INTERSECT",VERTEX,{"disambiguationData":[OD(1.0)],"derivedFrom":[sQuery(id+"F3.wireOp",EDGE,"E23.3"),subQ0]}),1.0]])],"derivedFrom":subQ0})])]});}
            var Q8;
            {var subQ0=sQuery(id+"F3.wireOp",EDGE,"E26");Q8=makeQuery(id+"F9.opExtrude","SWEPT_FACE",FACE,{"disambiguationData":[OSD([subQ0]),TDD([makeQuery(id+"F3.imprint","IMPRINT",EDGE,{"disambiguationData":[TD([[makeQuery(id+"F3.imprint","INTERSECT",VERTEX,{"disambiguationData":[OD(1.0)],"derivedFrom":[sQuery(id+"F3.wireOp",EDGE,"E23.4"),subQ0]}),1.0]])],"derivedFrom":subQ0})])]});}
            var Q9;
            {var subQ0=sQuery(id+"F3.wireOp",EDGE,"E26");Q9=makeQuery(id+"F9.opExtrude","SWEPT_FACE",FACE,{"disambiguationData":[OSD([subQ0]),TDD([makeQuery(id+"F3.imprint","IMPRINT",EDGE,{"disambiguationData":[TD([[makeQuery(id+"F3.imprint","INTERSECT",VERTEX,{"disambiguationData":[OD(0.0)],"derivedFrom":[sQuery(id+"F3.wireOp",EDGE,"E23.0"),subQ0]}),-1.0]])],"derivedFrom":subQ0})])]});}
            var Q10;
            {var subQ0=sQuery(id+"F3.wireOp",EDGE,"E26");Q10=makeQuery(id+"F9.opExtrude","SWEPT_FACE",FACE,{"disambiguationData":[OSD([subQ0]),TDD([makeQuery(id+"F3.imprint","IMPRINT",EDGE,{"disambiguationData":[TD([[makeQuery(id+"F3.imprint","INTERSECT",VERTEX,{"disambiguationData":[OD(1.0)],"derivedFrom":[sQuery(id+"F3.wireOp",EDGE,"E23.0"),subQ0]}),1.0]])],"derivedFrom":subQ0})])]});}
            fillet(context, id + "F11", {"entities" : qUnion([Q0, Q1, Q2, Q3, Q4, Q5, Q6, Q7, Q8, Q9, Q10]), "radius" : 1 * mm, "tangentPropagation" : true, "allowEdgeOverflow" : false});
        }
        {
            var Q0;
            Q0=qCreatedBy(makeId("Front.planeOp"),FACE);
            var sketch = newSketch(context, id + "F12", { "sketchPlane" : qUnion([Q0])});
            skLineSegment(sketch, "E28", {"start": v(0, 0) * mm, "end": v(0, 33.5) * mm, "construction": true});
            skLineSegment(sketch, "E29", {"start": v(0, 43.5) * mm, "end": v(-20, 43.5) * mm});
            skLineSegment(sketch, "E30", {"start": v(0, 33.5) * mm, "end": v(0, 43.5) * mm});
            skLineSegment(sketch, "E31", {"start": v(-20, 43.5) * mm, "end": v(-20, 33.5) * mm});
            skLineSegment(sketch, "E32", {"start": v(-20, 33.5) * mm, "end": v(0, 33.5) * mm});
            skLineSegment(sketch, "E33", {"start": v(-10, 43.5) * mm, "end": v(-10, 32.5) * mm, "construction": true});
            skCircle(sketch, "E34", {"center": v(-10, 32.5) * mm, "radius": 9 * mm});
            skLineSegment(sketch, "E35", {"start": v(-10, 32.5) * mm, "end": v(-10, 21.5) * mm, "construction": true});
            skLineSegment(sketch, "E36", {"start": v(-10, 21.5) * mm, "end": v(-20, 21.5) * mm});
            skLineSegment(sketch, "E37", {"start": v(-20, 21.5) * mm, "end": v(-20, 31.5) * mm});
            skLineSegment(sketch, "E38", {"start": v(-20, 31.5) * mm, "end": v(0, 31.5) * mm});
            skLineSegment(sketch, "E39", {"start": v(0, 31.5) * mm, "end": v(0, 21.5) * mm});
            skLineSegment(sketch, "E40", {"start": v(0, 21.5) * mm, "end": v(-10, 21.5) * mm});
            skLineSegment(sketch, "E41", {"start": v(-19, 32.5) * mm, "end": v(-10, 32.5) * mm});
            skLineSegment(sketch, "E42", {"start": v(-10, 32.5) * mm, "end": v(-1, 32.5) * mm});
            skSolve(sketch);
        }
        {
            var Q0;
            Q0=makeQuery(id+"F12.imprint","IMPRINT",FACE,{"disambiguationData":[TD([[makeQuery(id+"F12.imprint","IMPRINT",EDGE,{"derivedFrom":sQuery(id+"F12.wireOp",EDGE,"E29")}),1.0]])]});
            var Q1;
            Q1=makeQuery(id+"F12.imprint","IMPRINT",FACE,{"disambiguationData":[TD([[makeQuery(id+"F12.imprint","IMPRINT",EDGE,{"derivedFrom":sQuery(id+"F12.wireOp",EDGE,"E36")}),-1.0]])]});
            var Q2;
            Q2=sQuery(id+"F0.wireOp",EDGE,"E19");
            revolve(context, id + "F13", {"entities" : qUnion([Q0, Q1]), "axis" : qUnion([Q2]), "revolveType" : RevolveType.FULL});
        }
        {
            var Q0;
            {var subQ0=sQuery(id+"F12.wireOp",EDGE,"E34");var subQ1=sQuery(id+"F12.wireOp",EDGE,"E32");var subQ2=makeQuery(id+"F12.imprint","INTERSECT",VERTEX,{"disambiguationData":[OD(0.0)],"derivedFrom":[subQ1,subQ0]});Q0=makeQuery(id+"F12.imprint","IMPRINT",FACE,{"disambiguationData":[TD([[makeQuery(id+"F12.imprint","IMPRINT",EDGE,{"disambiguationData":[TD([[subQ2,-1.0]])],"derivedFrom":subQ1}),-1.0]])]});}
            var Q1;
            {var subQ0=sQuery(id+"F12.wireOp",EDGE,"E34");var subQ1=sQuery(id+"F12.wireOp",EDGE,"E32");var subQ2=makeQuery(id+"F12.imprint","INTERSECT",VERTEX,{"disambiguationData":[OD(0.0)],"derivedFrom":[subQ1,subQ0]});Q1=makeQuery(id+"F12.imprint","IMPRINT",FACE,{"disambiguationData":[TD([[makeQuery(id+"F12.imprint","IMPRINT",EDGE,{"disambiguationData":[TD([[subQ2,-1.0]])],"derivedFrom":subQ1}),1.0]])]});}
            var Q2;
            Q2=sQuery(id+"F12.wireOp",EDGE,"E41");
            revolve(context, id + "F14", {"entities" : qUnion([Q0, Q1]), "axis" : qUnion([Q2]), "revolveType" : RevolveType.FULL});
        }
        {
            var Q0;
            Q0=makeQuery(id+"F14.opRevolve","SWEPT_BODY",BODY,{"disambiguationData":[OSD([sQuery(id+"F12.wireOp",EDGE,"E34"),sQuery(id+"F12.wireOp",EDGE,"E41"),sQuery(id+"F12.wireOp",EDGE,"E42")])]});
            var Q1;
            Q1=sQuery(id+"F0.wireOp",EDGE,"E19");
            circularPattern(context, id + "F15", {"entities" : qUnion([Q0]), "axis" : qUnion([Q1]), "angle" : 360 * degree, "instanceCount" : 11, "equalSpace" : true});
        }
    });
